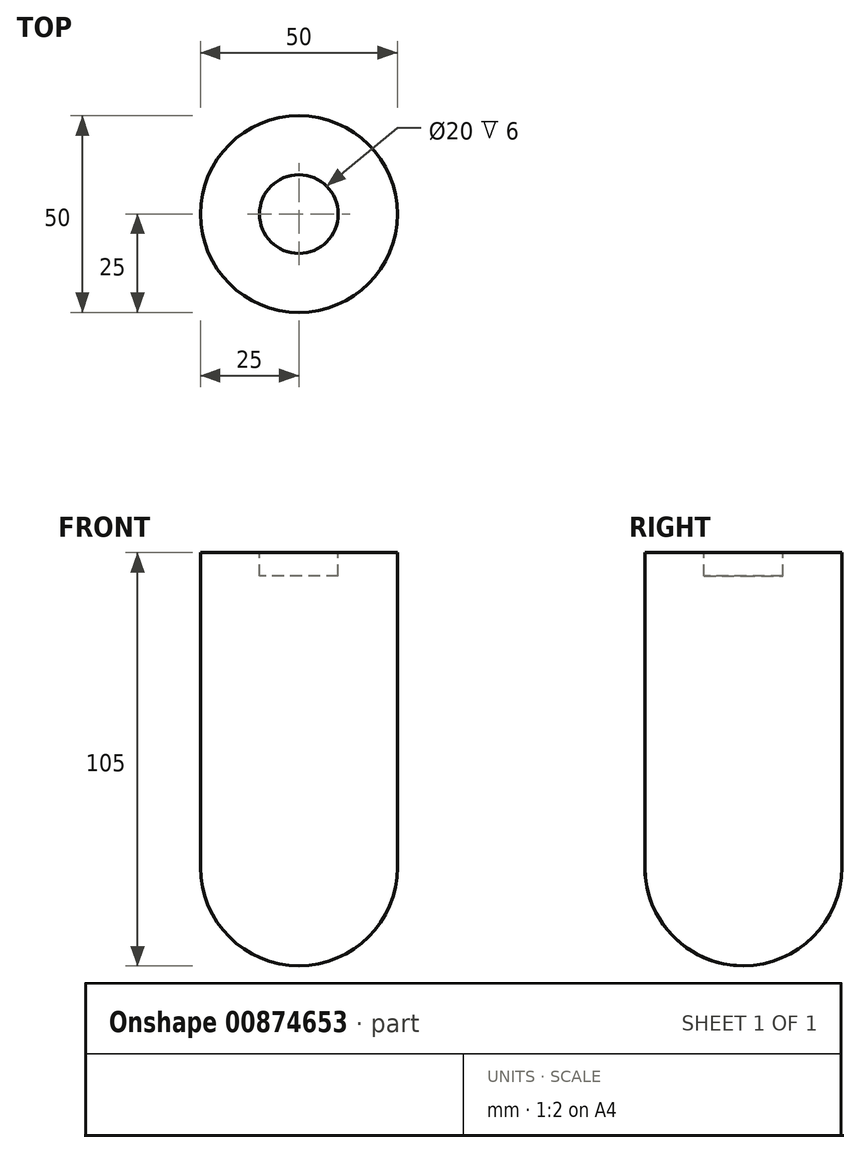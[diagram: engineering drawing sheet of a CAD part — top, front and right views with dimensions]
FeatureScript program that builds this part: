
annotation { "Feature Type Name" : "Feature", "Feature Type Description" : "" }
export const myFeature = defineFeature(function(context is Context, id is Id, definition is map)
    precondition{}
    {
        {
            var Q0;
            Q0=qCreatedBy(makeId("Top.planeOp"),FACE);
            var sketch = newSketch(context, id + "F0", { "sketchPlane" : qUnion([Q0])});
            skCircle(sketch, "E0", {"center": v(0, 0) * mm, "radius": 25 * mm});
            skSolve(sketch);
        }
        {
            var Q0;
            Q0 = qSketchRegion(id + "F0", true);
            extrude(context, id + "F1", {"entities" : qUnion([Q0]), "depth" : 80 * mm, "offsetDistance" : 25 * mm});
        }
        {
            var Q0;
            Q0=qCreatedBy(makeId("Right.planeOp"),FACE);
            var sketch = newSketch(context, id + "F2", { "sketchPlane" : qUnion([Q0])});
            skPoint(sketch, "E1", {"position": v(0, -25) * mm});
            skPoint(sketch, "E2", {"position": v(-25, 0) * mm});
            skArc(sketch, "E3", {"start": v(-25, 0) * mm, "mid": v(-17.68, -17.68) * mm, "end": v(0, -25) * mm});
            skLineSegment(sketch, "E4", {"start": v(0, -25) * mm, "end": v(0, 0) * mm});
            skLineSegment(sketch, "E5", {"start": v(0, 0) * mm, "end": v(-25, 0) * mm});
            skSolve(sketch);
        }
        {
            var Q0;
            Q0=makeQuery(id+"F2.imprint","IMPRINT",FACE,{"disambiguationData":[TD([[makeQuery(id+"F2.imprint","IMPRINT",EDGE,{"derivedFrom":sQuery(id+"F2.wireOp",EDGE,"E3")}),1.0]])]});
            var Q1;
            Q1=sQuery(id+"F2.wireOp",EDGE,"E4");
            revolve(context, id + "F3", {"operationType" : NewBodyOperationType.ADD, "surfaceOperationType" : NewSurfaceOperationType.NEW, "entities" : qUnion([Q0]), "axis" : qUnion([Q1]), "revolveType" : RevolveType.FULL});
        }
        {
            var Q0;
            Q0=qCreatedBy(makeId("Top.planeOp"),FACE);
            cPlane(context, id + "F4", {"entities" : qUnion([Q0]), "cplaneType" : CPlaneType.OFFSET, "offset" : 80 * mm, "width" : 150 * mm, "height" : 150 * mm});
        }
        {
            var Q0;
            Q0=qCreatedBy(id+"F4.planeOp",FACE);
            var sketch = newSketch(context, id + "F5", { "sketchPlane" : qUnion([Q0])});
            skCircle(sketch, "E6", {"center": v(0, 0) * mm, "radius": 10 * mm});
            skSolve(sketch);
        }
        {
            var Q0;
            Q0 = qSketchRegion(id + "F5", true);
            extrude(context, id + "F6", {"entities" : qUnion([Q0]), "operationType" : NewBodyOperationType.REMOVE, "oppositeDirection" : true, "depth" : 6 * mm, "offsetDistance" : 25 * mm});
        }
    });
